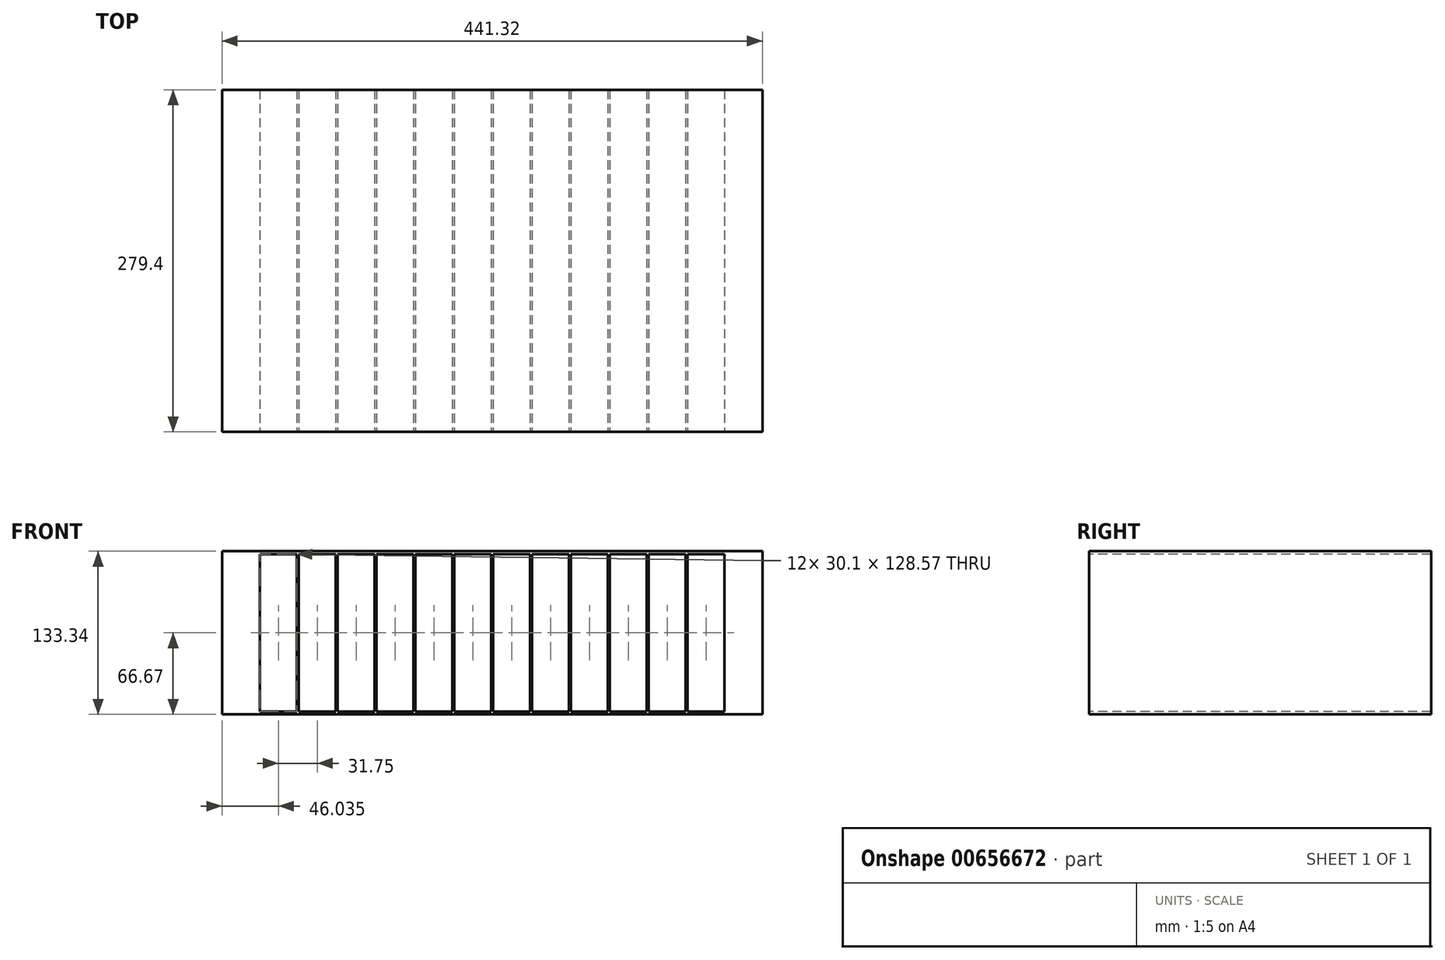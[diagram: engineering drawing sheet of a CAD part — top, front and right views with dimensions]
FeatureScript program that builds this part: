
annotation { "Feature Type Name" : "Feature", "Feature Type Description" : "" }
export const myFeature = defineFeature(function(context is Context, id is Id, definition is map)
    precondition{}
    {
        {
            var Q0;
            Q0=qCreatedBy(makeId("Front.planeOp"),FACE);
            var sketch = newSketch(context, id + "F0", { "sketchPlane" : qUnion([Q0])});
            skLineSegment(sketch, "E0.bottom", {"start": v(220.66, -66.67) * mm, "end": v(-220.66, -66.68) * mm});
            skLineSegment(sketch, "E0.top", {"start": v(220.66, 66.68) * mm, "end": v(-220.66, 66.67) * mm});
            skLineSegment(sketch, "E0.left", {"start": v(220.66, -66.67) * mm, "end": v(220.66, 66.68) * mm});
            skLineSegment(sketch, "E0.right", {"start": v(-220.66, -66.68) * mm, "end": v(-220.66, 66.67) * mm});
            skPoint(sketch, "E0.middle", {"position": v(15.87, 0) * mm});
            skLineSegment(sketch, "E1.bottom", {"start": v(30.92, -64.29) * mm, "end": v(0.83, -64.29) * mm});
            skLineSegment(sketch, "E1.top", {"start": v(30.92, 64.29) * mm, "end": v(0.83, 64.29) * mm});
            skLineSegment(sketch, "E1.left", {"start": v(30.92, -64.29) * mm, "end": v(30.92, 64.29) * mm});
            skCircle(sketch, "E2", {"center": v(15.87, 58.48) * mm, "radius": 3 * mm});
            skCircle(sketch, "E3.MirrorC", {"center": v(15.87, -58.48) * mm, "radius": 3 * mm});
            skLineSegment(sketch, "E4.1.0.0", {"start": v(62.67, -64.29) * mm, "end": v(32.58, -64.29) * mm});
            skLineSegment(sketch, "E4.1.0.1", {"start": v(62.67, 64.29) * mm, "end": v(32.58, 64.29) * mm});
            skPoint(sketch, "E4.1.0.2", {"position": v(47.63, 0) * mm});
            skLineSegment(sketch, "E4.1.0.3", {"start": v(62.67, -64.29) * mm, "end": v(62.67, 64.29) * mm});
            skLineSegment(sketch, "E4.1.0.4", {"start": v(32.58, -64.29) * mm, "end": v(32.58, 64.29) * mm});
            skPoint(sketch, "E4.1.0.5", {"position": v(47.63, 0) * mm});
            skCircle(sketch, "E4.1.0.6", {"center": v(47.62, -58.48) * mm, "radius": 3 * mm});
            skCircle(sketch, "E4.1.0.7", {"center": v(47.62, 58.48) * mm, "radius": 3 * mm});
            skLineSegment(sketch, "E4.2.0.0", {"start": v(94.42, -64.29) * mm, "end": v(64.33, -64.29) * mm});
            skLineSegment(sketch, "E4.2.0.1", {"start": v(94.42, 64.29) * mm, "end": v(64.33, 64.29) * mm});
            skPoint(sketch, "E4.2.0.2", {"position": v(79.38, 0) * mm});
            skLineSegment(sketch, "E4.2.0.3", {"start": v(94.42, -64.29) * mm, "end": v(94.42, 64.29) * mm});
            skLineSegment(sketch, "E4.2.0.4", {"start": v(64.33, -64.29) * mm, "end": v(64.33, 64.29) * mm});
            skPoint(sketch, "E4.2.0.5", {"position": v(79.38, 0) * mm});
            skCircle(sketch, "E4.2.0.6", {"center": v(79.38, -58.48) * mm, "radius": 3 * mm});
            skCircle(sketch, "E4.2.0.7", {"center": v(79.38, 58.48) * mm, "radius": 3 * mm});
            skLineSegment(sketch, "E4.3.0.0", {"start": v(126.17, -64.29) * mm, "end": v(96.08, -64.29) * mm});
            skLineSegment(sketch, "E4.3.0.1", {"start": v(126.17, 64.29) * mm, "end": v(96.08, 64.29) * mm});
            skPoint(sketch, "E4.3.0.2", {"position": v(111.13, 0) * mm});
            skLineSegment(sketch, "E4.3.0.3", {"start": v(126.17, -64.29) * mm, "end": v(126.17, 64.29) * mm});
            skLineSegment(sketch, "E4.3.0.4", {"start": v(96.08, -64.29) * mm, "end": v(96.08, 64.29) * mm});
            skPoint(sketch, "E4.3.0.5", {"position": v(111.13, 0) * mm});
            skCircle(sketch, "E4.3.0.6", {"center": v(111.13, -58.48) * mm, "radius": 3 * mm});
            skCircle(sketch, "E4.3.0.7", {"center": v(111.13, 58.48) * mm, "radius": 3 * mm});
            skLineSegment(sketch, "E4.4.0.0", {"start": v(157.92, -64.29) * mm, "end": v(127.83, -64.29) * mm});
            skLineSegment(sketch, "E4.4.0.1", {"start": v(157.92, 64.29) * mm, "end": v(127.83, 64.29) * mm});
            skPoint(sketch, "E4.4.0.2", {"position": v(142.88, 0) * mm});
            skLineSegment(sketch, "E4.4.0.3", {"start": v(157.92, -64.29) * mm, "end": v(157.92, 64.29) * mm});
            skLineSegment(sketch, "E4.4.0.4", {"start": v(127.83, -64.29) * mm, "end": v(127.83, 64.29) * mm});
            skPoint(sketch, "E4.4.0.5", {"position": v(142.88, 0) * mm});
            skCircle(sketch, "E4.4.0.6", {"center": v(142.88, -58.48) * mm, "radius": 3 * mm});
            skCircle(sketch, "E4.4.0.7", {"center": v(142.88, 58.48) * mm, "radius": 3 * mm});
            skLineSegment(sketch, "E4.5.0.0", {"start": v(189.67, -64.29) * mm, "end": v(159.58, -64.29) * mm});
            skLineSegment(sketch, "E4.5.0.1", {"start": v(189.67, 64.29) * mm, "end": v(159.58, 64.29) * mm});
            skPoint(sketch, "E4.5.0.2", {"position": v(174.63, 0) * mm});
            skLineSegment(sketch, "E4.5.0.3", {"start": v(189.67, -64.29) * mm, "end": v(189.67, 64.29) * mm});
            skLineSegment(sketch, "E4.5.0.4", {"start": v(159.58, -64.29) * mm, "end": v(159.58, 64.29) * mm});
            skPoint(sketch, "E4.5.0.5", {"position": v(174.63, 0) * mm});
            skCircle(sketch, "E4.5.0.6", {"center": v(174.63, -58.48) * mm, "radius": 3 * mm});
            skCircle(sketch, "E4.5.0.7", {"center": v(174.63, 58.48) * mm, "radius": 3 * mm});
            skLineSegment(sketch, "E4.direction1", {"start": v(0.83, -64.29) * mm, "end": v(32.58, -64.29) * mm, "construction": true});
            skCircle(sketch, "E5.MirrorC", {"center": v(-15.87, 58.48) * mm, "radius": 3 * mm});
            skCircle(sketch, "E6.MirrorC", {"center": v(-142.88, 58.48) * mm, "radius": 3 * mm});
            skCircle(sketch, "E7.MirrorC", {"center": v(-174.63, -58.48) * mm, "radius": 3 * mm});
            skLineSegment(sketch, "E8.MirrorCS", {"start": v(-127.83, -64.29) * mm, "end": v(-127.83, 64.29) * mm});
            skLineSegment(sketch, "E9.MirrorCS", {"start": v(-32.58, -64.29) * mm, "end": v(-32.58, 64.29) * mm});
            skCircle(sketch, "E10.MirrorC", {"center": v(-47.62, -58.48) * mm, "radius": 3 * mm});
            skCircle(sketch, "E11.MirrorC", {"center": v(-47.62, 58.48) * mm, "radius": 3 * mm});
            skLineSegment(sketch, "E12.MirrorCS", {"start": v(-30.92, -64.29) * mm, "end": v(-0.83, -64.29) * mm});
            skPoint(sketch, "E13.MirrorP", {"position": v(-111.13, 0) * mm});
            skCircle(sketch, "E14.MirrorC", {"center": v(-79.38, 58.48) * mm, "radius": 3 * mm});
            skPoint(sketch, "E15.MirrorP", {"position": v(-174.63, 0) * mm});
            skPoint(sketch, "E16.MirrorP", {"position": v(-79.38, 0) * mm});
            skCircle(sketch, "E17.MirrorC", {"center": v(-15.87, -58.48) * mm, "radius": 3 * mm});
            skCircle(sketch, "E18.MirrorC", {"center": v(-174.63, 58.48) * mm, "radius": 3 * mm});
            skLineSegment(sketch, "E19.MirrorCS", {"start": v(-96.08, -64.29) * mm, "end": v(-96.08, 64.29) * mm});
            skPoint(sketch, "E20.MirrorP", {"position": v(-15.87, 0) * mm});
            skPoint(sketch, "E21.MirrorP", {"position": v(-47.63, 0) * mm});
            skPoint(sketch, "E22.MirrorP", {"position": v(-142.88, 0) * mm});
            skCircle(sketch, "E23.MirrorC", {"center": v(-142.88, -58.48) * mm, "radius": 3 * mm});
            skLineSegment(sketch, "E24.MirrorCS", {"start": v(-64.33, -64.29) * mm, "end": v(-64.33, 64.29) * mm});
            skCircle(sketch, "E25.MirrorC", {"center": v(-111.13, 58.48) * mm, "radius": 3 * mm});
            skCircle(sketch, "E26.MirrorC", {"center": v(-111.13, -58.48) * mm, "radius": 3 * mm});
            skCircle(sketch, "E27.MirrorC", {"center": v(-79.38, -58.48) * mm, "radius": 3 * mm});
            skLineSegment(sketch, "E28.MirrorCS", {"start": v(-126.17, -64.29) * mm, "end": v(-126.17, 64.29) * mm});
            skLineSegment(sketch, "E29.MirrorCS", {"start": v(-94.42, 64.29) * mm, "end": v(-64.33, 64.29) * mm});
            skLineSegment(sketch, "E30.MirrorCS", {"start": v(-126.17, -64.29) * mm, "end": v(-96.08, -64.29) * mm});
            skLineSegment(sketch, "E31.MirrorCS", {"start": v(-157.92, -64.29) * mm, "end": v(-157.92, 64.29) * mm});
            skLineSegment(sketch, "E32.MirrorCS", {"start": v(-159.58, -64.29) * mm, "end": v(-159.58, 64.29) * mm});
            skLineSegment(sketch, "E33.MirrorCS", {"start": v(-157.92, -64.29) * mm, "end": v(-127.83, -64.29) * mm});
            skLineSegment(sketch, "E34.MirrorCS", {"start": v(-62.67, -64.29) * mm, "end": v(-32.58, -64.29) * mm});
            skLineSegment(sketch, "E35.MirrorCS", {"start": v(-62.67, 64.29) * mm, "end": v(-32.58, 64.29) * mm});
            skLineSegment(sketch, "E36.MirrorCS", {"start": v(-30.92, 64.29) * mm, "end": v(-0.83, 64.29) * mm});
            skLineSegment(sketch, "E37.MirrorCS", {"start": v(-189.67, -64.29) * mm, "end": v(-159.58, -64.29) * mm});
            skLineSegment(sketch, "E38.MirrorCS", {"start": v(-62.67, -64.29) * mm, "end": v(-62.67, 64.29) * mm});
            skLineSegment(sketch, "E39.MirrorCS", {"start": v(-94.42, -64.29) * mm, "end": v(-94.42, 64.29) * mm});
            skLineSegment(sketch, "E40.MirrorCS", {"start": v(-126.17, 64.29) * mm, "end": v(-96.08, 64.29) * mm});
            skLineSegment(sketch, "E41.MirrorCS", {"start": v(-189.67, 64.29) * mm, "end": v(-159.58, 64.29) * mm});
            skLineSegment(sketch, "E42.MirrorCS", {"start": v(-94.42, -64.29) * mm, "end": v(-64.33, -64.29) * mm});
            skLineSegment(sketch, "E43.MirrorCS", {"start": v(-30.92, -64.29) * mm, "end": v(-30.92, 64.29) * mm});
            skLineSegment(sketch, "E44.MirrorCS", {"start": v(-189.67, -64.29) * mm, "end": v(-189.67, 64.29) * mm});
            skLineSegment(sketch, "E45.MirrorCS", {"start": v(-157.92, 64.29) * mm, "end": v(-127.83, 64.29) * mm});
            skLineSegment(sketch, "E46.MirrorCS", {"start": v(-0.83, -64.29) * mm, "end": v(-32.58, -64.29) * mm, "construction": true});
            skLineSegment(sketch, "E47", {"start": v(-0.83, -64.29) * mm, "end": v(-0.83, 64.29) * mm});
            skLineSegment(sketch, "E48", {"start": v(0.83, 64.29) * mm, "end": v(0.83, -64.29) * mm});
            skSolve(sketch);
        }
        {
            var Q0;
            Q0=makeQuery(id+"F0.imprint","IMPRINT",FACE,{"disambiguationData":[TD([[makeQuery(id+"F0.imprint","IMPRINT",EDGE,{"derivedFrom":sQuery(id+"F0.wireOp",EDGE,"E0.bottom")}),-1.0]])]});
            extrude(context, id + "F1", {"entities" : qUnion([Q0]), "oppositeDirection" : true, "depth" : 279.4 * mm, "offsetDistance" : 25.4 * mm});
        }
    });
